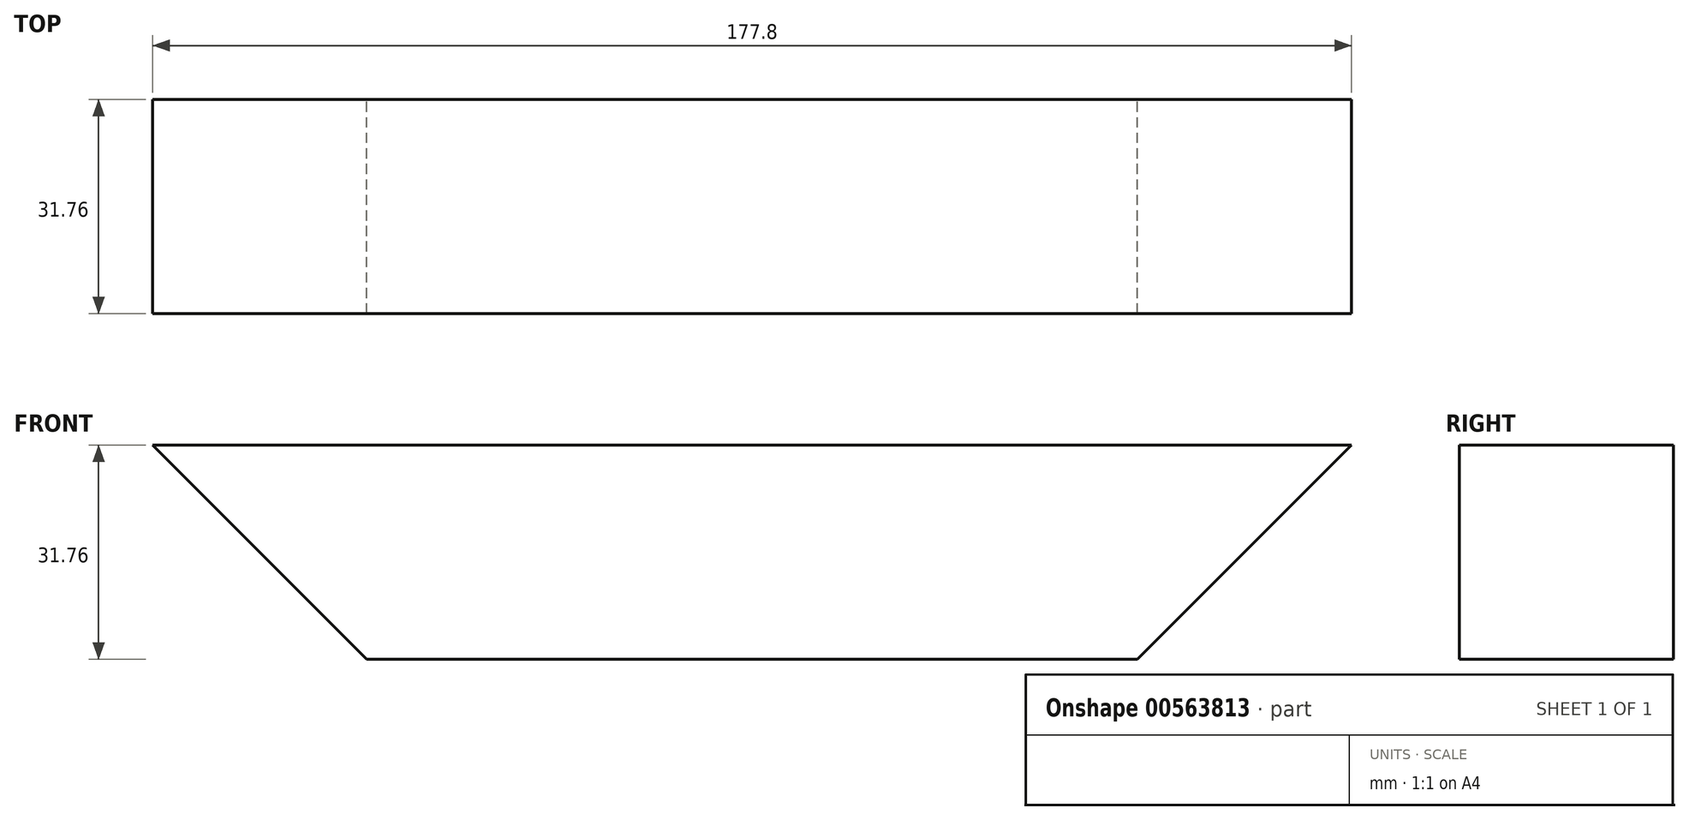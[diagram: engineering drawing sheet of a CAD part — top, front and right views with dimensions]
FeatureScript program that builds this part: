
annotation { "Feature Type Name" : "Feature", "Feature Type Description" : "" }
export const myFeature = defineFeature(function(context is Context, id is Id, definition is map)
    precondition{}
    {
        {
            var Q0;
            Q0=qCreatedBy(makeId("Front.planeOp"),FACE);
            var sketch = newSketch(context, id + "F0", { "sketchPlane" : qUnion([Q0])});
            skLineSegment(sketch, "E0.bottom", {"start": v(-88.9, 15.87) * mm, "end": v(88.9, 15.87) * mm});
            skLineSegment(sketch, "E0.top", {"start": v(-88.9, -15.88) * mm, "end": v(88.9, -15.88) * mm});
            skLineSegment(sketch, "E0.left", {"start": v(-88.9, 15.87) * mm, "end": v(-88.9, -15.88) * mm});
            skLineSegment(sketch, "E0.right", {"start": v(88.9, 15.87) * mm, "end": v(88.9, -15.88) * mm});
            skPoint(sketch, "E0.middle", {"position": v(0, 0) * mm});
            skLineSegment(sketch, "E1", {"start": v(-88.9, 15.87) * mm, "end": v(-57.15, -15.88) * mm});
            skLineSegment(sketch, "E2", {"start": v(88.9, 15.88) * mm, "end": v(57.15, -15.88) * mm});
            skSolve(sketch);
        }
        {
            var Q0;
            Q0=makeQuery(id+"F0.imprint","IMPRINT",FACE,{"disambiguationData":[TD([[makeQuery(id+"F0.imprint","IMPRINT",EDGE,{"derivedFrom":sQuery(id+"F0.wireOp",EDGE,"E0.bottom")}),-1.0]])]});
            extrude(context, id + "F1", {"entities" : qUnion([Q0]), "endBound" : BoundingType.SYMMETRIC, "depth" : 31.75 * mm, "offsetDistance" : 25.4 * mm});
        }
    });
